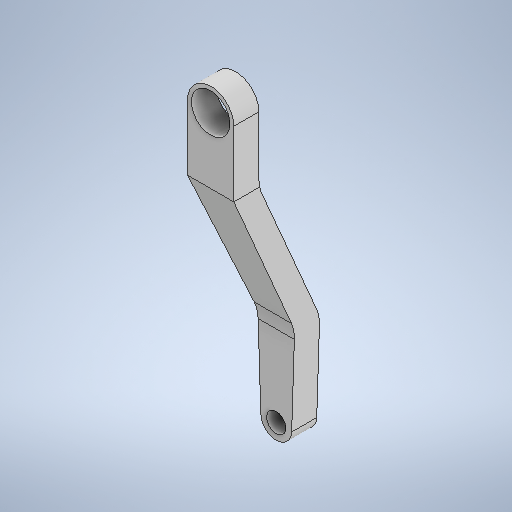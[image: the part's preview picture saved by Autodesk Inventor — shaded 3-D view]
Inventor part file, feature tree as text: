
AUTODESK INVENTOR PART (.ipt)
format: ipt  version: 2025.1 (Build 291241000, 241)  size: 317,440 bytes
history: native  units: mm
features: sketch x5, extrude x3, hole x2, fillet x1, projected_geometry x1
ambient origin geometry x8: Origin, YZ Plane, XZ Plane, XY Plane, X Axis, Y Axis, Z Axis, Center Point
bodies: Body1 (feature_tree)
feature tree (12):
  extrude  "Extrusion7"  Depth=10.0mm
  extrude  "Extrusion8"  Depth=17.0mm
  extrude  "Extrusion9"  Depth=23.0mm
  hole  "Hole1"  [1 undecoded]
  hole  "Hole2"  [1 undecoded]
  fillet  "Fillet1"  Radius=8.0mm
  sketch  "Sketch19"  dims[d79=10.0mm d80=10.0mm]
  sketch  "Sketch20"  dims[d82=6.5mm d83=17.0mm]
  sketch  "Sketch21"  dims[d84=25.0mm d85=23.0mm]
  projected_geometry  "Projected Loop13"
  sketch  "Sketch22"  dims[d86=37.940206mm d87=12.0mm d88=0.0mm]
  sketch  "Sketch23"  dims[d89=12.0mm d90=12.0mm d91=0.0mm d93=8.0mm d94=12.0mm d95=0.0mm d96=10.0mm d97=6.0mm d98=4.0mm d99=2.0mm d100=90.0deg d101=8.0mm d102=20.594885mm d103=5.0mm d104=6.0mm d105=4.0mm d106=2.0mm d107=90.0deg d108=8.0mm d109=20.594885mm d110=10.0mm d92=0.0mm]
note: 2 required parameter values undecoded (feature->parameter linkage not recoverable at this tier; creation-order binding heuristic only, values carry confidence <= 0.55)
